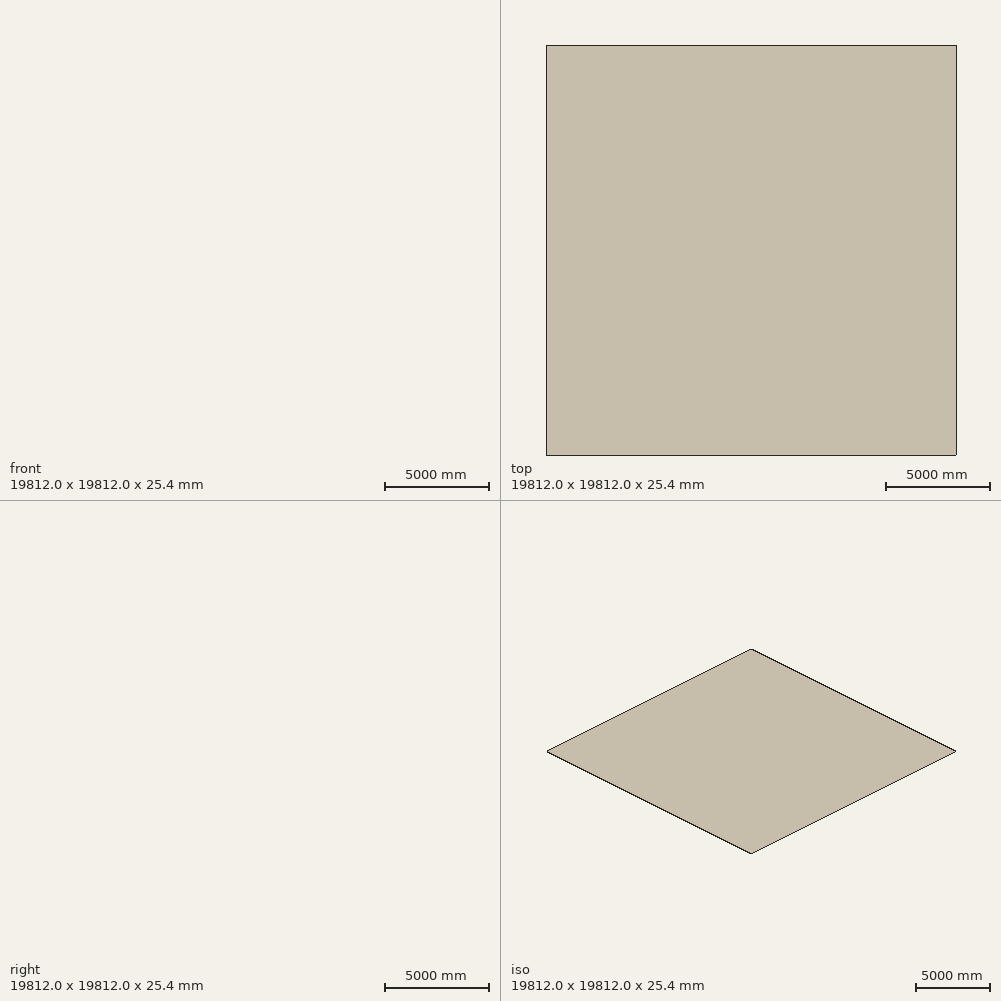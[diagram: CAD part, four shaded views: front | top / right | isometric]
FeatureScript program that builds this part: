
annotation { "Feature Type Name" : "Feature", "Feature Type Description" : "" }
export const myFeature = defineFeature(function(context is Context, id is Id, definition is map)
    precondition{}
    {
        {
            var Q0;
            Q0=qCreatedBy(makeId("Top.planeOp"),FACE);
            var sketch = newSketch(context, id + "F0", { "sketchPlane" : qUnion([Q0])});
            skLineSegment(sketch, "E0.bottom", {"start": v(-12732.3, 6071.92) * mm, "end": v(7079.7, 6071.92) * mm});
            skLineSegment(sketch, "E0.top", {"start": v(-12732.3, -13740.08) * mm, "end": v(7079.7, -13740.08) * mm});
            skLineSegment(sketch, "E0.left", {"start": v(-12732.3, 6071.92) * mm, "end": v(-12732.3, -13740.08) * mm});
            skLineSegment(sketch, "E0.right", {"start": v(7079.7, 6071.92) * mm, "end": v(7079.7, -13740.08) * mm});
            skSolve(sketch);
        }
        {
            var Q0;
            Q0 = qSketchRegion(id + "F0", true);
            extrude(context, id + "F1", {"entities" : qUnion([Q0]), "depth" : 25.4 * mm, "offsetDistance" : 25.4 * mm});
        }
    });
